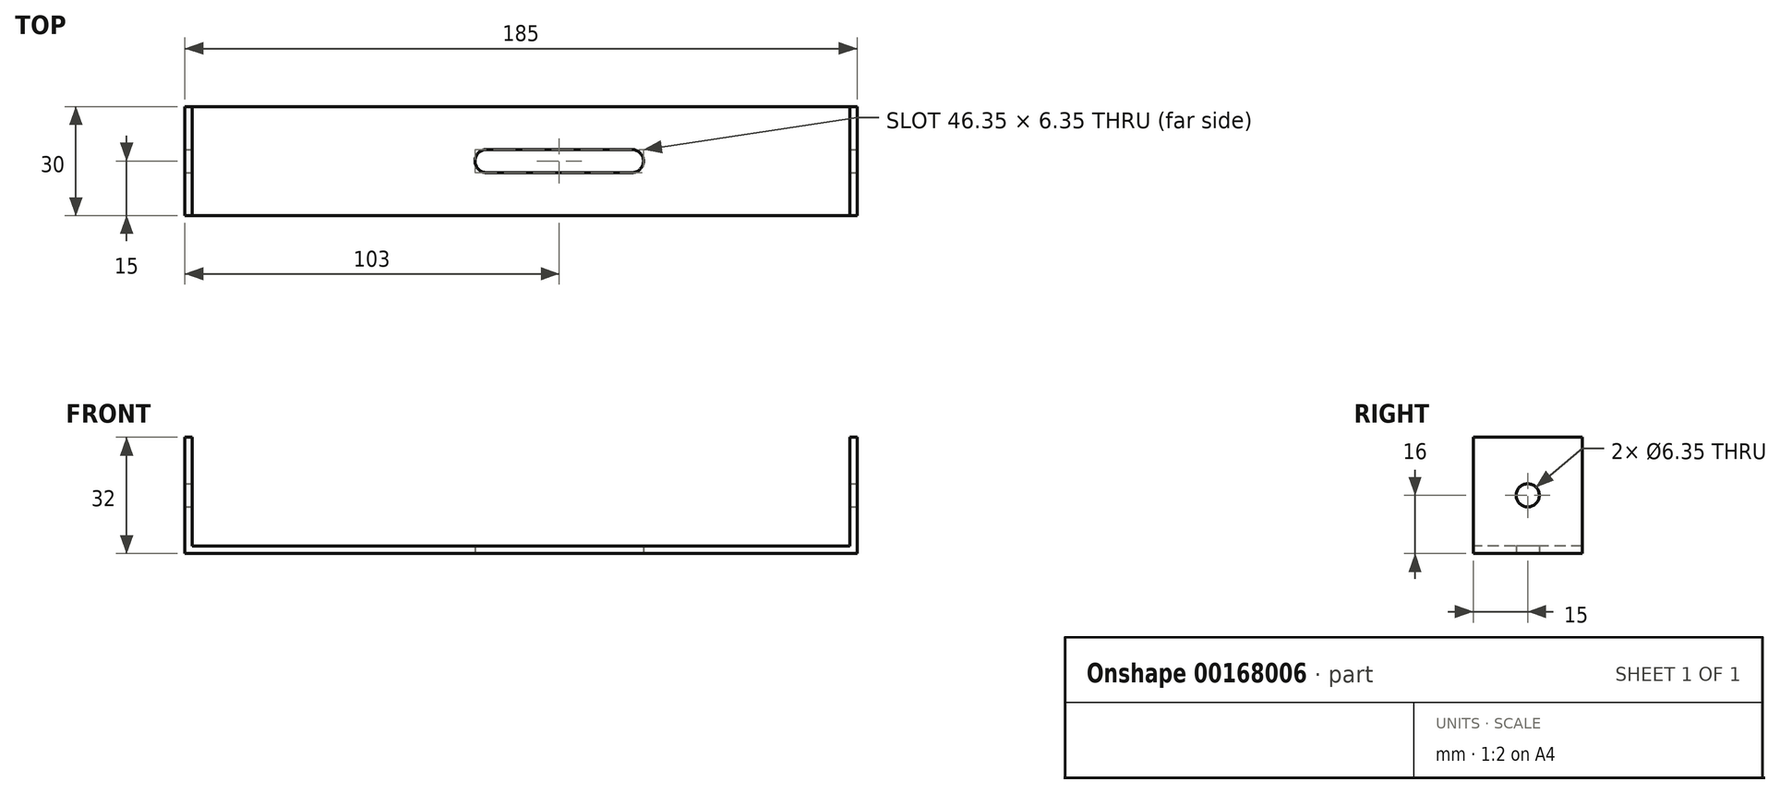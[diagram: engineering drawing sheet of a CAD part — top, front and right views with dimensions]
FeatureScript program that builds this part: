
annotation { "Feature Type Name" : "Feature", "Feature Type Description" : "" }
export const myFeature = defineFeature(function(context is Context, id is Id, definition is map)
    precondition{}
    {
        {
            var Q0;
            Q0=qCreatedBy(makeId("Right.planeOp"),FACE);
            var sketch = newSketch(context, id + "F0", { "sketchPlane" : qUnion([Q0])});
            skLineSegment(sketch, "E0.bottom", {"start": v(15, -1) * mm, "end": v(-15, -1) * mm});
            skLineSegment(sketch, "E0.top", {"start": v(15, 1) * mm, "end": v(-15, 1) * mm});
            skLineSegment(sketch, "E0.left", {"start": v(15, -1) * mm, "end": v(15, 1) * mm});
            skLineSegment(sketch, "E0.right", {"start": v(-15, -1) * mm, "end": v(-15, 1) * mm});
            skPoint(sketch, "E0.middle", {"position": v(0, 0) * mm});
            skLineSegment(sketch, "E1", {"start": v(-15, 1) * mm, "end": v(-15, 31) * mm});
            skLineSegment(sketch, "E2", {"start": v(-15, 31) * mm, "end": v(15, 31) * mm});
            skLineSegment(sketch, "E3", {"start": v(15, 31) * mm, "end": v(15, 1) * mm});
            skSolve(sketch);
        }
        {
            var Q0;
            Q0=makeQuery(id+"F0.imprint","IMPRINT",FACE,{"disambiguationData":[TD([[makeQuery(id+"F0.imprint","IMPRINT",EDGE,{"derivedFrom":sQuery(id+"F0.wireOp",EDGE,"E0.bottom")}),-1.0]])]});
            extrude(context, id + "F1", {"entities" : qUnion([Q0]), "depth" : 185 * mm, "symmetric" : true});
        }
        {
            var Q0;
            Q0=makeQuery(id+"F1.opExtrude","CAP_FACE",FACE,{"disambiguationData":[OSD([sQuery(id+"F0.wireOp",EDGE,"E0.bottom"),sQuery(id+"F0.wireOp",EDGE,"E0.top"),sQuery(id+"F0.wireOp",EDGE,"E0.left"),sQuery(id+"F0.wireOp",EDGE,"E0.right")])],"isStart":false});
            var sketch = newSketch(context, id + "F2", { "sketchPlane" : qUnion([Q0])});
            skLineSegment(sketch, "E4.0.0", {"start": v(-15, 1) * mm, "end": v(15, 1) * mm});
            skLineSegment(sketch, "E4.0.1", {"start": v(15, 1) * mm, "end": v(15, 31) * mm});
            skLineSegment(sketch, "E4.0.2", {"start": v(15, 31) * mm, "end": v(-15, 31) * mm});
            skLineSegment(sketch, "E4.0.3", {"start": v(-15, 31) * mm, "end": v(-15, 1) * mm});
            skSolve(sketch);
        }
        {
            var Q0;
            Q0 = qSketchRegion(id + "F2", true);
            extrude(context, id + "F3", {"entities" : qUnion([Q0]), "operationType" : NewBodyOperationType.ADD, "oppositeDirection" : true, "depth" : 2 * mm});
        }
        {
            var Q0;
            Q0=makeQuery(id+"F1.opExtrude","CAP_FACE",FACE,{"disambiguationData":[OSD([sQuery(id+"F0.wireOp",EDGE,"E0.bottom"),sQuery(id+"F0.wireOp",EDGE,"E0.top"),sQuery(id+"F0.wireOp",EDGE,"E0.left"),sQuery(id+"F0.wireOp",EDGE,"E0.right")])],"isStart":true});
            var sketch = newSketch(context, id + "F4", { "sketchPlane" : qUnion([Q0])});
            skLineSegment(sketch, "E5.0.0", {"start": v(15, 1) * mm, "end": v(-15, 1) * mm});
            skLineSegment(sketch, "E5.0.1", {"start": v(-15, 1) * mm, "end": v(-15, 31) * mm});
            skLineSegment(sketch, "E5.0.2", {"start": v(-15, 31) * mm, "end": v(15, 31) * mm});
            skLineSegment(sketch, "E5.0.3", {"start": v(15, 31) * mm, "end": v(15, 1) * mm});
            skSolve(sketch);
        }
        {
            var Q0;
            Q0 = qSketchRegion(id + "F4", true);
            extrude(context, id + "F5", {"entities" : qUnion([Q0]), "operationType" : NewBodyOperationType.ADD, "oppositeDirection" : true, "depth" : 2 * mm});
        }
        {
            var Q0;
            Q0=makeQuery(id+"F3.boolean.opBoolean","MERGE",FACE,{"derivedFrom":[makeQuery(id+"F1.opExtrude","CAP_FACE",FACE,{"disambiguationData":[OSD([sQuery(id+"F0.wireOp",EDGE,"E0.bottom"),sQuery(id+"F0.wireOp",EDGE,"E0.top"),sQuery(id+"F0.wireOp",EDGE,"E0.left"),sQuery(id+"F0.wireOp",EDGE,"E0.right")])],"isStart":false}),makeQuery(id+"F3.opExtrude","CAP_FACE",FACE,{"disambiguationData":[OSD([sQuery(id+"F2.wireOp",EDGE,"E4.0.0"),sQuery(id+"F2.wireOp",EDGE,"E4.0.1"),sQuery(id+"F2.wireOp",EDGE,"E4.0.2"),sQuery(id+"F2.wireOp",EDGE,"E4.0.3")])],"isStart":true})]});
            var sketch = newSketch(context, id + "F6", { "sketchPlane" : qUnion([Q0])});
            skCircle(sketch, "E6", {"center": v(0, 15) * mm, "radius": 3.18 * mm});
            skPoint(sketch, "E6.centerSnap0", {"position": v(-15, 15) * mm});
            skPoint(sketch, "E6.centerSnap1", {"position": v(0, -1) * mm});
            skSolve(sketch);
        }
        {
            var Q0;
            Q0 = qSketchRegion(id + "F6", true);
            extrude(context, id + "F7", {"entities" : qUnion([Q0]), "operationType" : NewBodyOperationType.REMOVE, "oppositeDirection" : true, "depth" : 250 * mm});
        }
        {
            var Q0;
            Q0=makeQuery(id+"F1.opExtrude","SWEPT_FACE",FACE,{"disambiguationData":[OSD([sQuery(id+"F0.wireOp",EDGE,"E0.bottom")])]});
            var sketch = newSketch(context, id + "F8", { "sketchPlane" : qUnion([Q0])});
            skLineSegment(sketch, "E7.0", {"start": v(-92.5, -15) * mm, "end": v(-92.5, 15) * mm});
            skCircle(sketch, "E8", {"center": v(30.5, 0) * mm, "radius": 3.18 * mm});
            skPoint(sketch, "E8.centerSnap0", {"position": v(-92.5, 0) * mm});
            skCircle(sketch, "E9", {"center": v(-9.5, 0) * mm, "radius": 3.17 * mm});
            skLineSegment(sketch, "E10", {"start": v(-9.5, -3.18) * mm, "end": v(30.5, -3.18) * mm});
            skLineSegment(sketch, "E11", {"start": v(30.5, 3.18) * mm, "end": v(-9.5, 3.18) * mm});
            skSolve(sketch);
        }
        {
            var Q0;
            Q0 = qSketchRegion(id + "F8", true);
            extrude(context, id + "F9", {"entities" : qUnion([Q0]), "operationType" : NewBodyOperationType.REMOVE, "oppositeDirection" : true, "depth" : 25 * mm});
        }
    });
